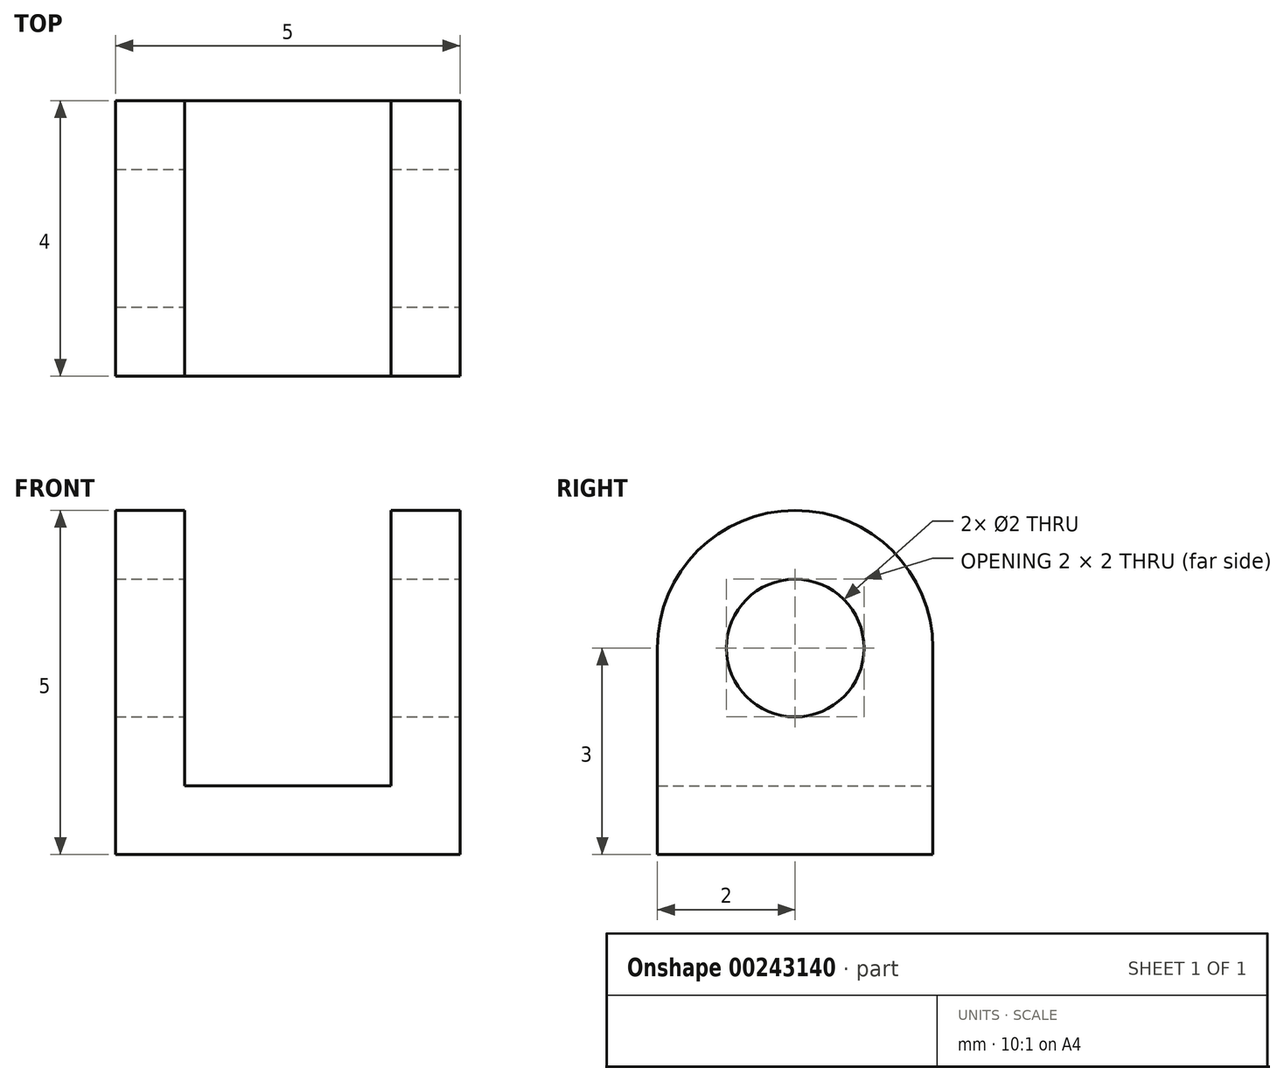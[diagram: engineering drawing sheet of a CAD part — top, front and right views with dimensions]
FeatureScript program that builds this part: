
annotation { "Feature Type Name" : "Feature", "Feature Type Description" : "" }
export const myFeature = defineFeature(function(context is Context, id is Id, definition is map)
    precondition{}
    {
        {
            var Q0;
            Q0=qCreatedBy(makeId("Front.planeOp"),FACE);
            var sketch = newSketch(context, id + "F0", { "sketchPlane" : qUnion([Q0])});
            skLineSegment(sketch, "E0", {"start": v(0, 0) * mm, "end": v(0, 3) * mm});
            skLineSegment(sketch, "E1", {"start": v(0, 3) * mm, "end": v(1, 3) * mm});
            skLineSegment(sketch, "E2", {"start": v(1, 3) * mm, "end": v(1, 1) * mm});
            skLineSegment(sketch, "E3", {"start": v(1, 1) * mm, "end": v(4, 1) * mm});
            skLineSegment(sketch, "E4", {"start": v(4, 1) * mm, "end": v(4, 3) * mm});
            skLineSegment(sketch, "E5", {"start": v(4, 3) * mm, "end": v(5, 3) * mm});
            skLineSegment(sketch, "E6", {"start": v(5, 3) * mm, "end": v(5, 0) * mm});
            skLineSegment(sketch, "E7", {"start": v(5, 0) * mm, "end": v(0, 0) * mm});
            skSolve(sketch);
        }
        {
            var Q0;
            Q0 = qSketchRegion(id + "F0", true);
            extrude(context, id + "F1", {"entities" : qUnion([Q0]), "depth" : 4 * mm});
        }
        {
            var Q0;
            Q0=makeQuery(id+"F1.opExtrude","SWEPT_FACE",FACE,{"disambiguationData":[OSD([sQuery(id+"F0.wireOp",EDGE,"E2")])]});
            var sketch = newSketch(context, id + "F2", { "sketchPlane" : qUnion([Q0])});
            skArc(sketch, "E8", {"start": v(0, 3) * mm, "mid": v(-2, 5) * mm, "end": v(-4, 3) * mm});
            skLineSegment(sketch, "E9", {"start": v(-4, 3) * mm, "end": v(0, 3) * mm});
            skSolve(sketch);
        }
        {
            var Q0;
            Q0 = qSketchRegion(id + "F2", true);
            extrude(context, id + "F3", {"entities" : qUnion([Q0]), "operationType" : NewBodyOperationType.ADD, "oppositeDirection" : true, "depth" : 1 * mm});
        }
        {
            var Q0;
            Q0=makeQuery(id+"F1.opExtrude","SWEPT_FACE",FACE,{"disambiguationData":[OSD([sQuery(id+"F0.wireOp",EDGE,"E6")])]});
            var sketch = newSketch(context, id + "F4", { "sketchPlane" : qUnion([Q0])});
            skArc(sketch, "E10", {"start": v(0, 3) * mm, "mid": v(-2, 5) * mm, "end": v(-4, 3) * mm});
            skLineSegment(sketch, "E11", {"start": v(-4, 3) * mm, "end": v(0, 3) * mm});
            skSolve(sketch);
        }
        {
            var Q0;
            Q0 = qSketchRegion(id + "F4", true);
            extrude(context, id + "F5", {"entities" : qUnion([Q0]), "operationType" : NewBodyOperationType.ADD, "oppositeDirection" : true, "depth" : 1 * mm});
        }
        {
            var Q0;
            Q0=makeQuery(id+"F5.boolean.opBoolean","MERGE",FACE,{"derivedFrom":[makeQuery(id+"F1.opExtrude","SWEPT_FACE",FACE,{"disambiguationData":[OSD([sQuery(id+"F0.wireOp",EDGE,"E6")])]}),makeQuery(id+"F5.opExtrude","CAP_FACE",FACE,{"disambiguationData":[OSD([sQuery(id+"F4.wireOp",EDGE,"E10"),sQuery(id+"F4.wireOp",EDGE,"E11")])],"isStart":true})]});
            var sketch = newSketch(context, id + "F6", { "sketchPlane" : qUnion([Q0])});
            skCircle(sketch, "E12", {"center": v(-2, 3) * mm, "radius": 1 * mm});
            skSolve(sketch);
        }
        {
            var Q0;
            Q0 = qSketchRegion(id + "F6", true);
            extrude(context, id + "F7", {"entities" : qUnion([Q0]), "operationType" : NewBodyOperationType.REMOVE, "oppositeDirection" : true, "depth" : 6 * mm});
        }
    });
